# Revit family: hansgrohe_71651187-Hansgrohe-Basic-set-for-single_
name_source: partatom
category: Plumbing Fixtures
revit_build: Autodesk Revit 2015 (Build: 20140322_1515(x64)
units: mm (PartAtom-declared; Revit-internal decimal feet)

## types (1)
- n.a.
    Brand url = http://www.hansgrohe-int.com
    Default Elevation = 1219.2 mm  [stored 4 ft]
    Design country = Germany
    Edition number = 1
    GTIN code = https://4059625293515
    Manufacturer country = Germany
    Manufacturer name = hansgrohe
    Material main = Chrome
    Product Guid = c818d5d8-d697-41a9-81a0-aee48bc7e89e
    Product SKU = 71651187
    Product certification = https://www.hansgrohe.com.cn
    Product data url = https://bimobject.com
    Product family = Concealed Basic set bath/shower mixers
    Product group = Hansgrohe
    Product name = 71651187 Hansgrohe Basic set for single lever shower mixer for concealed installation
    Product url = https://www.hansgrohe.com.cn
    QR code = http://bimobject.com
    Technical description = https://www.hansgrohe.com.cn

note: [stored X ft] marks values corroborated as IEEE doubles in the binary element streams (Revit-internal decimal feet)

## geometry (parser evidence)
native form markers: Sweep x2
no freeform markers — native parametric forms only
